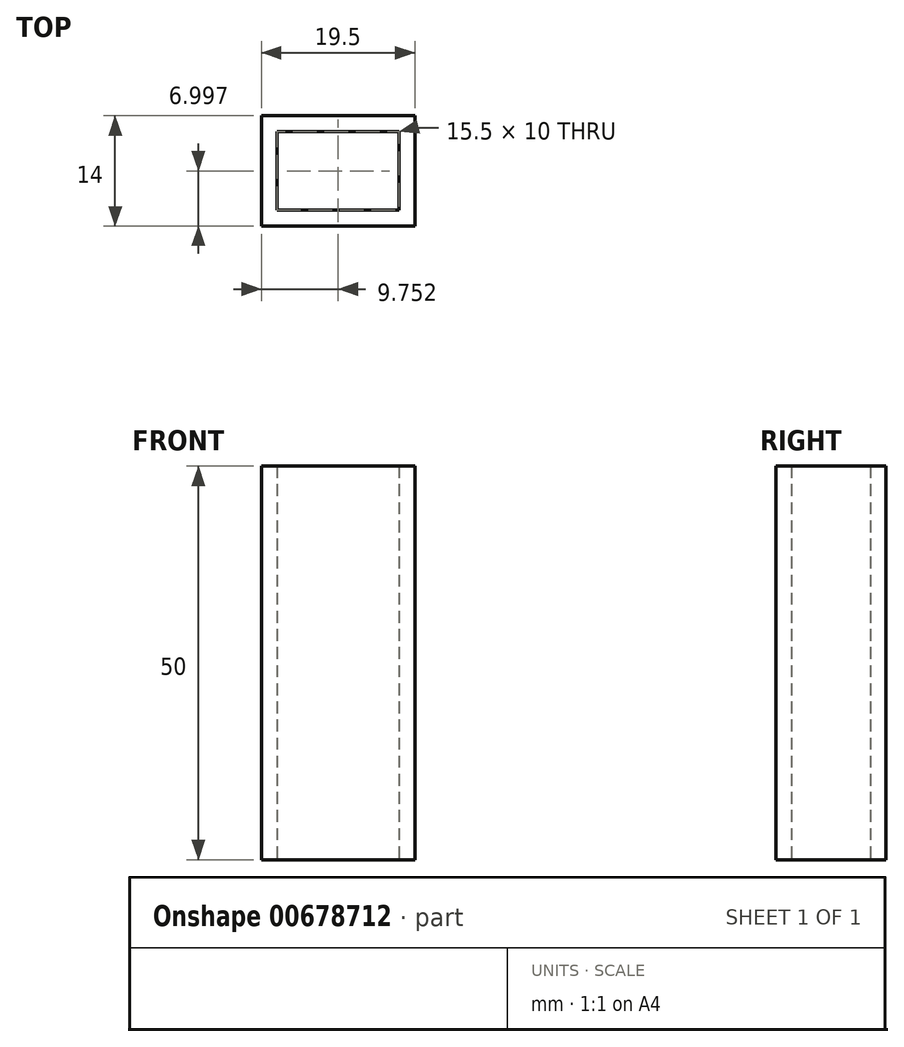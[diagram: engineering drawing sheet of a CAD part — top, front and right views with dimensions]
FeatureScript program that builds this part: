
annotation { "Feature Type Name" : "Feature", "Feature Type Description" : "" }
export const myFeature = defineFeature(function(context is Context, id is Id, definition is map)
    precondition{}
    {
        {
            var Q0;
            Q0=qCreatedBy(makeId("Top.planeOp"),FACE);
            var sketch = newSketch(context, id + "F0", { "sketchPlane" : qUnion([Q0])});
            skLineSegment(sketch, "E0.bottom", {"start": v(-3.82, 5.39) * mm, "end": v(15.68, 5.39) * mm});
            skLineSegment(sketch, "E0.top", {"start": v(-3.82, -8.61) * mm, "end": v(15.68, -8.61) * mm});
            skLineSegment(sketch, "E0.left", {"start": v(-3.82, 5.39) * mm, "end": v(-3.82, -8.61) * mm});
            skLineSegment(sketch, "E0.right", {"start": v(15.68, 5.39) * mm, "end": v(15.68, -8.61) * mm});
            skLineSegment(sketch, "E1.0", {"start": v(-1.82, 3.39) * mm, "end": v(13.68, 3.39) * mm});
            skLineSegment(sketch, "E1.1", {"start": v(-1.82, 3.39) * mm, "end": v(-1.82, -6.61) * mm});
            skLineSegment(sketch, "E1.2", {"start": v(-1.82, -6.61) * mm, "end": v(13.68, -6.61) * mm});
            skLineSegment(sketch, "E1.3", {"start": v(13.68, 3.39) * mm, "end": v(13.68, -6.61) * mm});
            skSolve(sketch);
        }
        {
            var Q0;
            Q0=makeQuery(id+"F0.imprint","IMPRINT",FACE,{"disambiguationData":[TD([[makeQuery(id+"F0.imprint","IMPRINT",EDGE,{"derivedFrom":sQuery(id+"F0.wireOp",EDGE,"E0.bottom")}),-1.0]])]});
            extrude(context, id + "F1", {"entities" : qUnion([Q0]), "depth" : 50 * mm, "offsetDistance" : 25 * mm});
        }
    });
